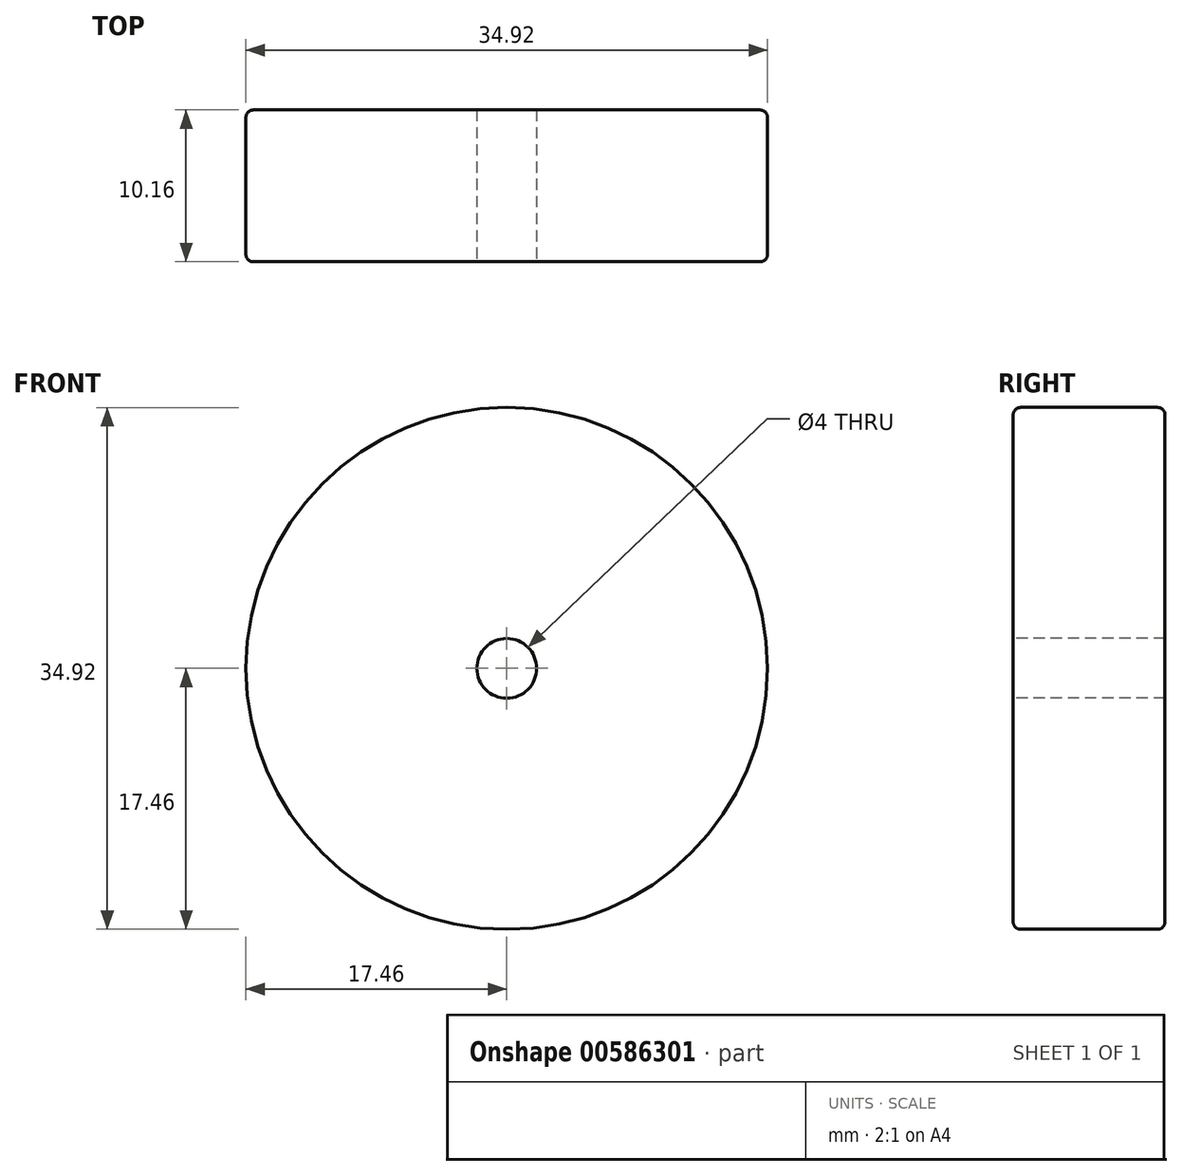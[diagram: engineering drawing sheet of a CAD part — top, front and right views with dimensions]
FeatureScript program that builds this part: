
annotation { "Feature Type Name" : "Feature", "Feature Type Description" : "" }
export const myFeature = defineFeature(function(context is Context, id is Id, definition is map)
    precondition{}
    {
        {
            var Q0;
            Q0=qCreatedBy(makeId("Front.planeOp"),FACE);
            var sketch = newSketch(context, id + "F0", { "sketchPlane" : qUnion([Q0])});
            skCircle(sketch, "E0", {"center": v(0, 0) * mm, "radius": 17.46 * mm});
            skSolve(sketch);
        }
        {
            var Q0;
            Q0=makeQuery(id+"F0.imprint","IMPRINT",FACE,{"disambiguationData":[TD([[makeQuery(id+"F0.imprint","IMPRINT",EDGE,{"derivedFrom":sQuery(id+"F0.wireOp",EDGE,"E0")}),1.0]])]});
            extrude(context, id + "F1", {"entities" : qUnion([Q0]), "depth" : 10.16 * mm, "offsetDistance" : 25.4 * mm});
        }
        {
            var Q0;
            Q0=makeQuery(id+"F1.opExtrude","CAP_FACE",FACE,{"disambiguationData":[OSD([sQuery(id+"F0.wireOp",EDGE,"E0")])],"isStart":false});
            var sketch = newSketch(context, id + "F2", { "sketchPlane" : qUnion([Q0])});
            skCircle(sketch, "E1", {"center": v(0, 0) * mm, "radius": 2 * mm});
            skSolve(sketch);
        }
        {
            var Q0;
            Q0=makeQuery(id+"F2.imprint","IMPRINT",FACE,{"disambiguationData":[TD([[makeQuery(id+"F2.imprint","IMPRINT",EDGE,{"derivedFrom":sQuery(id+"F2.wireOp",EDGE,"E1")}),1.0]])]});
            extrude(context, id + "F3", {"entities" : qUnion([Q0]), "operationType" : NewBodyOperationType.REMOVE, "oppositeDirection" : true, "depth" : 25.4 * mm, "offsetDistance" : 25.4 * mm});
        }
        {
            var Q0;
            Q0=makeQuery(id+"F1.opExtrude","CAP_EDGE",EDGE,{"disambiguationData":[OSD([sQuery(id+"F0.wireOp",EDGE,"E0")])],"isStart":false});
            var Q1;
            Q1=makeQuery(id+"F1.opExtrude","CAP_EDGE",EDGE,{"disambiguationData":[OSD([sQuery(id+"F0.wireOp",EDGE,"E0")])],"isStart":true});
            fillet(context, id + "F4", {"entities" : qUnion([Q0, Q1]), "radius" : 0.5 * mm, "allowEdgeOverflow" : false});
        }
    });
